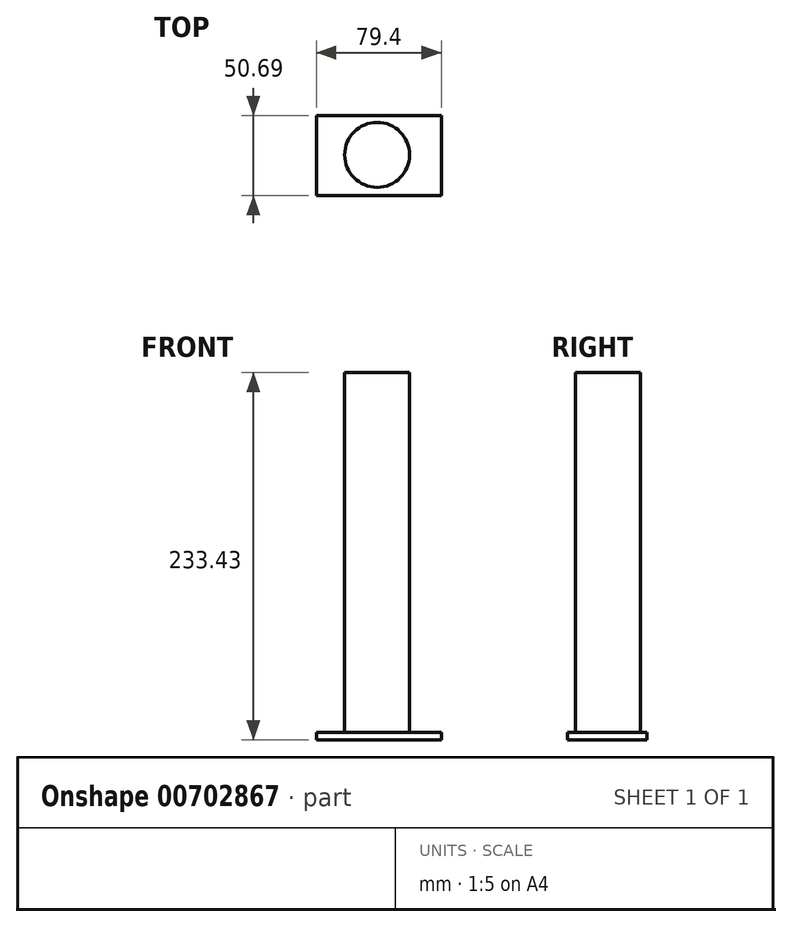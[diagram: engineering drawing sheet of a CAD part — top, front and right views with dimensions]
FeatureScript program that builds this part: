
annotation { "Feature Type Name" : "Feature", "Feature Type Description" : "" }
export const myFeature = defineFeature(function(context is Context, id is Id, definition is map)
    precondition{}
    {
        {
            var Q0;
            Q0=qCreatedBy(makeId("Top.planeOp"),FACE);
            var sketch = newSketch(context, id + "F0", { "sketchPlane" : qUnion([Q0])});
            skCircle(sketch, "E0", {"center": v(-19.25, 12.55) * mm, "radius": 20.63 * mm});
            skSolve(sketch);
        }
        {
            var Q0;
            Q0=makeQuery(id+"F0.imprint","IMPRINT",FACE,{"disambiguationData":[TD([[makeQuery(id+"F0.imprint","IMPRINT",EDGE,{"derivedFrom":sQuery(id+"F0.wireOp",EDGE,"E0")}),1.0]])]});
            extrude(context, id + "F1", {"entities" : qUnion([Q0]), "depth" : 228.6 * mm, "offsetDistance" : 25.4 * mm});
        }
        {
            var Q0;
            Q0=qCreatedBy(makeId("Top.planeOp"),FACE);
            var sketch = newSketch(context, id + "F2", { "sketchPlane" : qUnion([Q0])});
            skLineSegment(sketch, "E1.bottom", {"start": v(-57.86, -13.2) * mm, "end": v(21.54, -13.2) * mm});
            skLineSegment(sketch, "E1.top", {"start": v(-57.86, 37.5) * mm, "end": v(21.54, 37.5) * mm});
            skLineSegment(sketch, "E1.left", {"start": v(-57.86, -13.2) * mm, "end": v(-57.86, 37.5) * mm});
            skLineSegment(sketch, "E1.right", {"start": v(21.54, -13.2) * mm, "end": v(21.54, 37.5) * mm});
            skSolve(sketch);
        }
        {
            var Q0;
            Q0=makeQuery(id+"F2.imprint","IMPRINT",FACE,{"disambiguationData":[TD([[makeQuery(id+"F2.imprint","IMPRINT",EDGE,{"derivedFrom":sQuery(id+"F2.wireOp",EDGE,"E1.bottom")}),1.0]])]});
            extrude(context, id + "F3", {"entities" : qUnion([Q0]), "operationType" : NewBodyOperationType.ADD, "oppositeDirection" : true, "depth" : 4.83 * mm, "offsetDistance" : 25.4 * mm});
        }
    });
